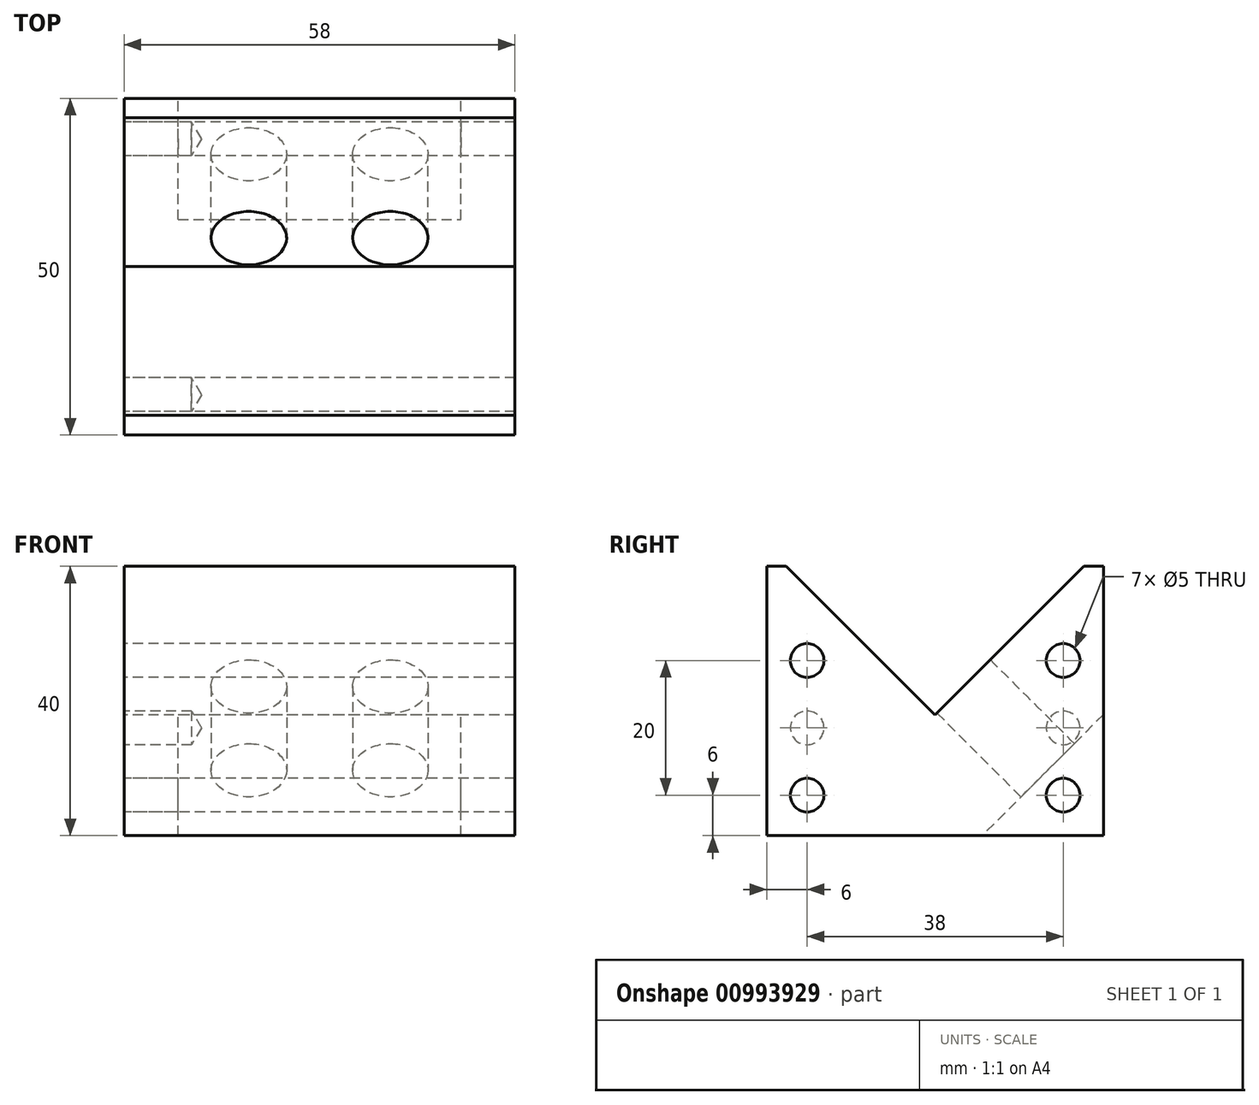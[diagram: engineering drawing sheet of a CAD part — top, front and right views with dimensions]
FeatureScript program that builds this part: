
annotation { "Feature Type Name" : "Feature", "Feature Type Description" : "" }
export const myFeature = defineFeature(function(context is Context, id is Id, definition is map)
    precondition{}
    {
        {
            var Q0;
            Q0=qCreatedBy(makeId("Right.planeOp"),FACE);
            var sketch = newSketch(context, id + "F0", { "sketchPlane" : qUnion([Q0])});
            skLineSegment(sketch, "E0", {"start": v(-25, 20) * mm, "end": v(-25, -20) * mm});
            skLineSegment(sketch, "E1", {"start": v(-25, -20) * mm, "end": v(25, -20) * mm});
            skLineSegment(sketch, "E2", {"start": v(25, -20) * mm, "end": v(25, 20) * mm});
            skLineSegment(sketch, "E3", {"start": v(22.1, 20) * mm, "end": v(0, -2.1) * mm});
            skLineSegment(sketch, "E4", {"start": v(0, -2.1) * mm, "end": v(-22.1, 20) * mm});
            skLineSegment(sketch, "E5", {"start": v(-25, 20) * mm, "end": v(-22.1, 20) * mm});
            skLineSegment(sketch, "E6", {"start": v(22.1, 20) * mm, "end": v(25, 20) * mm});
            skSolve(sketch);
        }
        {
            var Q0;
            Q0=makeQuery(id+"F0.imprint","IMPRINT",FACE,{"disambiguationData":[TD([[makeQuery(id+"F0.imprint","IMPRINT",EDGE,{"derivedFrom":sQuery(id+"F0.wireOp",EDGE,"E0")}),1.0]])]});
            extrude(context, id + "F1", {"entities" : qUnion([Q0]), "endBound" : BoundingType.SYMMETRIC, "depth" : 58 * mm, "offsetDistance" : 25 * mm});
        }
        {
            var Q0;
            Q0=qCreatedBy(makeId("Right.planeOp"),FACE);
            var sketch = newSketch(context, id + "F2", { "sketchPlane" : qUnion([Q0])});
            skLineSegment(sketch, "E7.0", {"start": v(25, -20) * mm, "end": v(25, -2) * mm});
            skLineSegment(sketch, "E8.0", {"start": v(7, -20) * mm, "end": v(25, -20) * mm});
            skLineSegment(sketch, "E9", {"start": v(25, -2) * mm, "end": v(7, -20) * mm});
            skPoint(sketch, "E10.orphan", {"position": v(25, 20) * mm});
            skPoint(sketch, "E11.orphan", {"position": v(-25, -20) * mm});
            skSolve(sketch);
        }
        {
            var Q0;
            Q0 = qSketchRegion(id + "F2", true);
            extrude(context, id + "F3", {"entities" : qUnion([Q0]), "operationType" : NewBodyOperationType.REMOVE, "endBound" : BoundingType.SYMMETRIC, "oppositeDirection" : true, "depth" : 42 * mm, "offsetDistance" : 25 * mm});
        }
        {
            var Q0;
            Q0=makeQuery(id+"F1.opExtrude","CAP_FACE",FACE,{"disambiguationData":[OSD([sQuery(id+"F0.wireOp",EDGE,"E0"),sQuery(id+"F0.wireOp",EDGE,"E1"),sQuery(id+"F0.wireOp",EDGE,"E2"),sQuery(id+"F0.wireOp",EDGE,"E3"),sQuery(id+"F0.wireOp",EDGE,"E4"),sQuery(id+"F0.wireOp",EDGE,"E5"),sQuery(id+"F0.wireOp",EDGE,"E6")])],"isStart":true});
            var sketch = newSketch(context, id + "F4", { "sketchPlane" : qUnion([Q0])});
            skPoint(sketch, "E12", {"position": v(-19, 6) * mm});
            skPoint(sketch, "E13", {"position": v(-19, -14) * mm});
            skPoint(sketch, "E14", {"position": v(19, -14) * mm});
            skPoint(sketch, "E15", {"position": v(19, 6) * mm});
            skPoint(sketch, "E16", {"position": v(-19, -4) * mm});
            skPoint(sketch, "E17", {"position": v(19, -4) * mm});
            skSolve(sketch);
        }
        {
            var Q0;
            Q0=sQuery(id+"F4.wireOp",VERTEX,"E13");
            var Q1;
            Q1=sQuery(id+"F4.wireOp",VERTEX,"E14");
            var Q2;
            Q2=makeQuery(id+"F1.opExtrude","SWEPT_BODY",BODY,{"disambiguationData":[OSD([sQuery(id+"F0.wireOp",EDGE,"E0"),sQuery(id+"F0.wireOp",EDGE,"E1"),sQuery(id+"F0.wireOp",EDGE,"E2"),sQuery(id+"F0.wireOp",EDGE,"E3"),sQuery(id+"F0.wireOp",EDGE,"E4"),sQuery(id+"F0.wireOp",EDGE,"E5"),sQuery(id+"F0.wireOp",EDGE,"E6")])]});
            hole(context, id + "F5", {"style" : HoleStyle.SIMPLE, "endStyle" : HoleEndStyle.THROUGH, "standardTappedOrClearance" : lookupTablePath({ "standard" : "ISO", "engagement" : "75%", "pitch" : "1 mm", "size" : "M6", "type" : "Tapped" }), "standardBlindInLast" : lookupTablePath({ "standard" : "ISO", "fit" : "Normal", "engagement" : "75%", "pitch" : "1 mm", "size" : "M6", "type" : "Clearance & tapped" }), "holeDiameter" : 5 * mm, "majorDiameter" : 6 * mm, "showTappedDepth" : true, "isTappedThrough" : true, "tappedDepth" : 8 * mm, "tapClearance" : 3, "locations" : qUnion([Q0, Q1]), "scope" : qUnion([Q2])});
        }
        {
            var Q0;
            Q0=sQuery(id+"F4.wireOp",VERTEX,"E12");
            var Q1;
            Q1=sQuery(id+"F4.wireOp",VERTEX,"E15");
            var Q2;
            Q2=makeQuery(id+"F1.opExtrude","SWEPT_BODY",BODY,{"disambiguationData":[OSD([sQuery(id+"F0.wireOp",EDGE,"E0"),sQuery(id+"F0.wireOp",EDGE,"E1"),sQuery(id+"F0.wireOp",EDGE,"E2"),sQuery(id+"F0.wireOp",EDGE,"E3"),sQuery(id+"F0.wireOp",EDGE,"E4"),sQuery(id+"F0.wireOp",EDGE,"E5"),sQuery(id+"F0.wireOp",EDGE,"E6")])]});
            hole(context, id + "F6", {"style" : HoleStyle.SIMPLE, "endStyle" : HoleEndStyle.THROUGH, "standardTappedOrClearance" : lookupTablePath({ "standard" : "ISO", "engagement" : "75%", "pitch" : "1 mm", "size" : "M6", "type" : "Tapped" }), "standardBlindInLast" : lookupTablePath({ "standard" : "ISO", "fit" : "Normal", "engagement" : "75%", "pitch" : "1 mm", "size" : "M6", "type" : "Clearance & tapped" }), "holeDiameter" : 5 * mm, "majorDiameter" : 6 * mm, "showTappedDepth" : true, "tappedDepth" : 8 * mm, "tapClearance" : 3, "locations" : qUnion([Q0, Q1]), "scope" : qUnion([Q2])});
        }
        {
            var Q0;
            Q0=sQuery(id+"F4.wireOp",VERTEX,"E16");
            var Q1;
            Q1=sQuery(id+"F4.wireOp",VERTEX,"E17");
            var Q2;
            Q2=makeQuery(id+"F1.opExtrude","SWEPT_BODY",BODY,{"disambiguationData":[OSD([sQuery(id+"F0.wireOp",EDGE,"E0"),sQuery(id+"F0.wireOp",EDGE,"E1"),sQuery(id+"F0.wireOp",EDGE,"E2"),sQuery(id+"F0.wireOp",EDGE,"E3"),sQuery(id+"F0.wireOp",EDGE,"E4"),sQuery(id+"F0.wireOp",EDGE,"E5"),sQuery(id+"F0.wireOp",EDGE,"E6")])]});
            hole(context, id + "F7", {"style" : HoleStyle.SIMPLE, "endStyle" : HoleEndStyle.BLIND, "holeDiameter" : 5 * mm, "majorDiameter" : 6 * mm, "holeDepth" : 10 * mm, "tappedDepth" : 8 * mm, "tapClearance" : 3, "locations" : qUnion([Q0, Q1]), "scope" : qUnion([Q2])});
        }
        {
            var Q0;
            Q0=makeQuery(id+"F3.boolean.opBoolean","COPY",FACE,{"derivedFrom":makeQuery(id+"F3.opExtrude","SWEPT_FACE",FACE,{"disambiguationData":[OSD([sQuery(id+"F2.wireOp",EDGE,"E9")])]})});
            var sketch = newSketch(context, id + "F8", { "sketchPlane" : qUnion([Q0])});
            skPoint(sketch, "E18", {"position": v(-10.5, 4.52) * mm});
            skPoint(sketch, "E19", {"position": v(10.5, 4.52) * mm});
            skSolve(sketch);
        }
        {
            var Q0;
            Q0=sQuery(id+"F8.wireOp",VERTEX,"E18");
            var Q1;
            Q1=sQuery(id+"F8.wireOp",VERTEX,"E19");
            var Q2;
            Q2=makeQuery(id+"F1.opExtrude","SWEPT_BODY",BODY,{"disambiguationData":[OSD([sQuery(id+"F0.wireOp",EDGE,"E0"),sQuery(id+"F0.wireOp",EDGE,"E1"),sQuery(id+"F0.wireOp",EDGE,"E2"),sQuery(id+"F0.wireOp",EDGE,"E3"),sQuery(id+"F0.wireOp",EDGE,"E4"),sQuery(id+"F0.wireOp",EDGE,"E5"),sQuery(id+"F0.wireOp",EDGE,"E6")])]});
            hole(context, id + "F9", {"style" : HoleStyle.SIMPLE, "endStyle" : HoleEndStyle.THROUGH, "standardTappedOrClearance" : lookupTablePath({ "standard" : "ISO", "engagement" : "50%", "pitch" : "1.25 mm", "size" : "M12", "type" : "Tapped" }), "standardBlindInLast" : lookupTablePath({ "standard" : "ISO", "fit" : "Normal", "engagement" : "50%", "pitch" : "1.25 mm", "size" : "M12", "type" : "Clearance & tapped" }), "holeDiameter" : 11.2 * mm, "majorDiameter" : 12 * mm, "showTappedDepth" : true, "isTappedThrough" : true, "tappedDepth" : 15 * mm, "tapClearance" : 3, "startFromSketch" : true, "locations" : qUnion([Q0, Q1]), "scope" : qUnion([Q2])});
        }
    });
